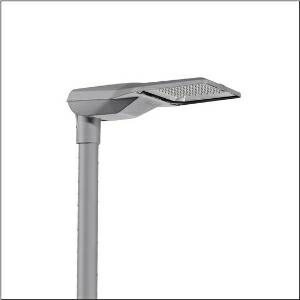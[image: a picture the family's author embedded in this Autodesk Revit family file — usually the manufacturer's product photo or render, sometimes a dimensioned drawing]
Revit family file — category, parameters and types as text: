
# Revit family: streetlight_sl_21_iq_midi___st0_8a_5xe3c41d08nb_52df
name_source: partatom
category: Lighting Fixtures
units: mm (PartAtom-declared; Revit-internal decimal feet)

## family parameters
Cut with Voids When Loaded = No
Host = Face
Light Source = No
Part Type = Normal
Room Calculation Point = No
Round Connector Dimension = Use Diameter
Shared = No

## types (1)
- --- (1 x LED, 24250 lm, 155.5 W, 4000K)
    Apparent Load = 155 VA
    CIE Flux Codes = 41 75 97 100 100
    Color Rendering = 70
    Color Temperature = 4000K
    Default Elevation = 1800 mm
    Description = Streetlight SL 21 iQ midi, mast luminaire, primary light control with lens, of PMMA, primary optical cover: cover, of toughened safety glass, transparent, light distribution: ST0.8a, light emission: direct distribution, primary light characteristic: asymmetric, installation type: post-top, side-entry, LED, High Power LED, rated luminous flux: 24.250lm, luminous efficacy: 156lm/W, light colour: 740, colour temperature: 4000K, control gear: iQ-Comfort, control: Auto-Match, Temp-Guard, Lumen-Switch, Night-Set, Smart-Wire, Light-Fading, Desk-Remote (wireless, voltage-free reading and setting of iQ features in the workshop via application-optimized NFC function/RFID function), optimised constant luminous flux control (CLO 2.0), pre-setting: linear dimming characteristic, mains connection: 230..240V, AC, 50/60Hz, start of lifetime: 156W, end of service life: 162W, reduction: 69W, luminaire housing, of diecast aluminium, powder-coated, Siteco® metallic grey (DB 702S), corrosivity category C5 mid according to DIN EN ISO 12944, please order mast flange separately, inclination adjustable: 0°, 5°, 10°, 15°, sealing non-destructively replaceable, multi-level sealing system, length: 644mm, width: 335mm, height: 110mm, mast flange for spigot size: 42mm (side-entry): 5XC10008XM4, 60/48mm (side-entry/post-top): 5XC10108XM2, 76/60mm (side-entry/post-top): 5XC10108XM1, mounting height: 4..8m, protection rating (complete): IP66, insulation class (complete): insulation class II (safety insulation), certification: CE, ENEC, ENEC+, VDE, impact resistance: IK10, permissible operating ambient temperature for outdoor applications: -40..+50°C, standard-compliant lighting for roads and squares, packaging unit: 1 piece

Light Distribution: ST0.8a
    Height = 111 mm
    Lamp = 1 x LED
    Lamp Light Flux = 24250 lm
    Lamp Power = 155.5 W
    Lamp count = 1
    Length = 644 mm
    Luminous efficacy = 156 lm/W
    Manufacturer = Siteco
    ModVariant = No
    Model = 5XE3C41D08NB
    Number of Poles = 1
    OnlyDefault = Yes
    Power Factor = 1
    Product Name = Streetlight SL 21 iQ midi | ST0.8a
    Product group = mast luminaire | pylon top
    ProductGroupID = 6100
    Protection Class = Protection class II
    Protection Degree = IP 66
    RLX_Detail_Level = 1
    RLX_Emergency_Light_Flux = 0 lm
    RLX_Emergency_Type = 0
    RLX_Emergency_Type_DB = No
    RlxData = <blob elided: 27213 chars, md5=45cf4a9e>
    Socket = socket
    Standby Power = 0 W
    System Light Flux = 24250 lm
    System Power = 155 W
    Type Comments = factory setting: luminous flux: 100 % | dim-lin: 254 | 823 mA
    Type Image = l_1004298.jpg
    URL = http://relux.com
    VarID = @adj_168916
    Voltage = 0 V
    Weight = 0.00 kg
    Width = 336 mm

## geometry (parser evidence)
native form markers: Blend x4, Sweep x9
no freeform markers — native parametric forms only
